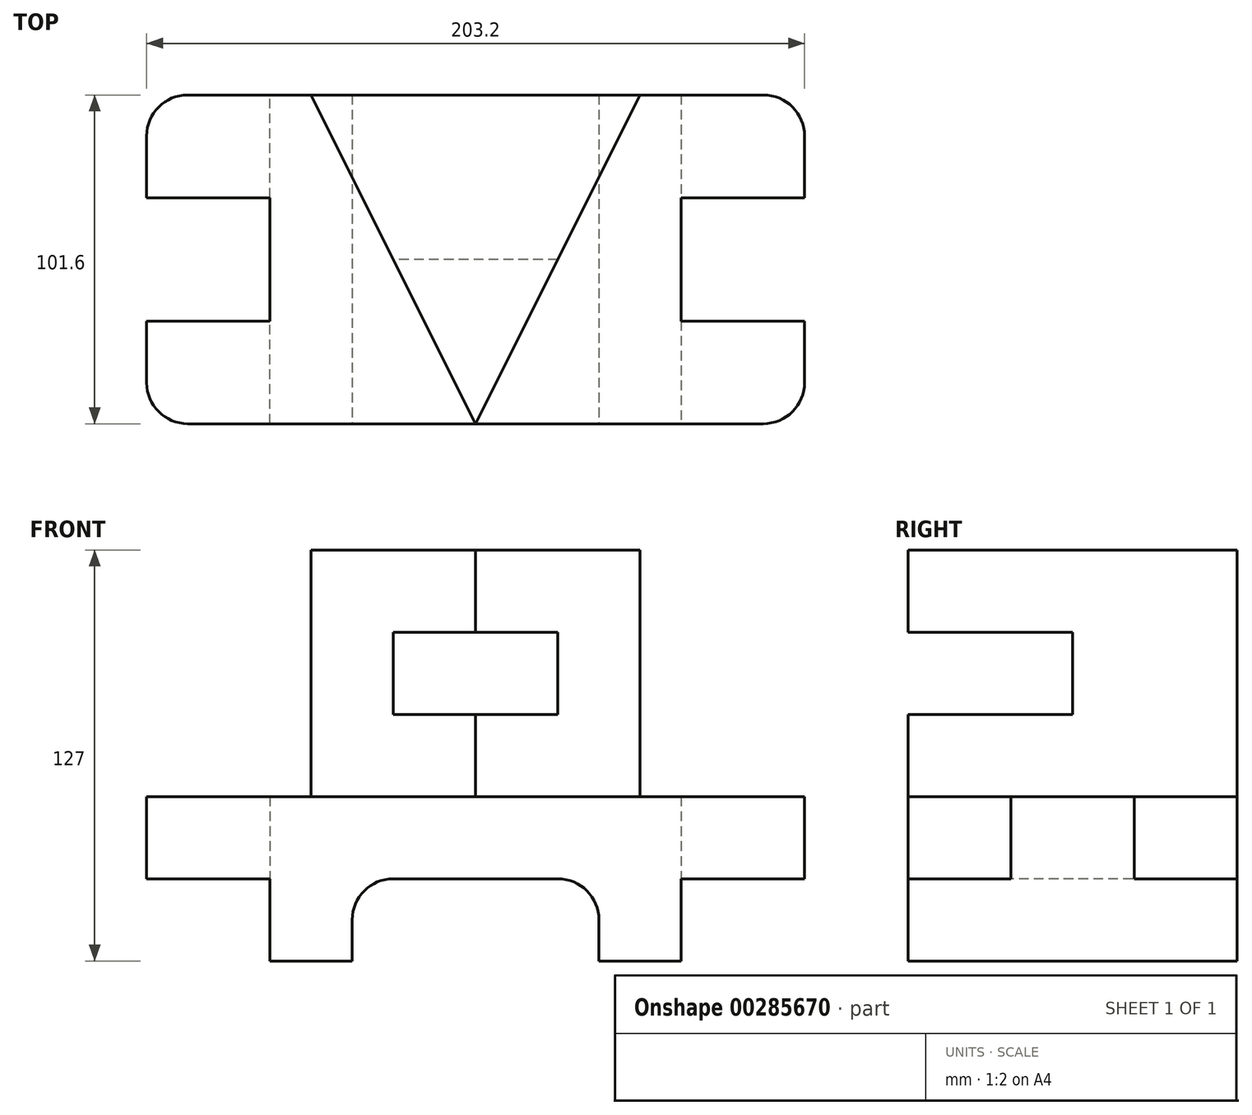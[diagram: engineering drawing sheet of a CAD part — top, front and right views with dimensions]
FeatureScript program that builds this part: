
annotation { "Feature Type Name" : "Feature", "Feature Type Description" : "" }
export const myFeature = defineFeature(function(context is Context, id is Id, definition is map)
    precondition{}
    {
        {
            var Q0;
            Q0=qCreatedBy(makeId("Top.planeOp"),FACE);
            var sketch = newSketch(context, id + "F0", { "sketchPlane" : qUnion([Q0])});
            skLineSegment(sketch, "E0", {"start": v(0, 0) * mm, "end": v(177.8, 0) * mm});
            skLineSegment(sketch, "E1", {"start": v(0, 0) * mm, "end": v(0, 31.75) * mm});
            skLineSegment(sketch, "E2", {"start": v(0, 31.75) * mm, "end": v(25.4, 31.75) * mm});
            skLineSegment(sketch, "E3", {"start": v(25.4, 31.75) * mm, "end": v(25.4, 69.85) * mm});
            skLineSegment(sketch, "E4", {"start": v(25.4, 69.85) * mm, "end": v(0, 69.85) * mm});
            skLineSegment(sketch, "E5", {"start": v(0, 69.85) * mm, "end": v(0, 101.6) * mm});
            skLineSegment(sketch, "E6", {"start": v(0, 101.6) * mm, "end": v(177.8, 101.6) * mm});
            skLineSegment(sketch, "E7", {"start": v(177.8, 101.6) * mm, "end": v(177.8, 69.85) * mm});
            skLineSegment(sketch, "E8", {"start": v(177.8, 69.85) * mm, "end": v(152.4, 69.85) * mm});
            skLineSegment(sketch, "E9", {"start": v(152.4, 69.85) * mm, "end": v(152.4, 31.75) * mm});
            skLineSegment(sketch, "E10", {"start": v(152.4, 31.75) * mm, "end": v(177.8, 31.75) * mm});
            skLineSegment(sketch, "E11", {"start": v(177.8, 31.75) * mm, "end": v(177.8, 0) * mm});
            skLineSegment(sketch, "E12", {"start": v(0, 31.75) * mm, "end": v(-12.7, 31.75) * mm});
            skLineSegment(sketch, "E13", {"start": v(-12.7, 31.75) * mm, "end": v(-12.7, 12.7) * mm});
            skLineSegment(sketch, "E14", {"start": v(177.8, 31.75) * mm, "end": v(190.5, 31.75) * mm});
            skPoint(sketch, "E14.endSnap0", {"position": v(165.1, 31.75) * mm});
            skLineSegment(sketch, "E15", {"start": v(190.5, 31.75) * mm, "end": v(190.5, 12.7) * mm});
            skLineSegment(sketch, "E16", {"start": v(177.8, 69.85) * mm, "end": v(190.5, 69.85) * mm});
            skLineSegment(sketch, "E17", {"start": v(0, 69.85) * mm, "end": v(-12.7, 69.85) * mm});
            skLineSegment(sketch, "E18", {"start": v(-12.7, 69.85) * mm, "end": v(-12.7, 88.9) * mm});
            skLineSegment(sketch, "E19", {"start": v(190.5, 69.85) * mm, "end": v(190.5, 88.9) * mm});
            skArc(sketch, "E20", {"start": v(0, 101.6) * mm, "mid": v(-8.98, 97.88) * mm, "end": v(-12.7, 88.9) * mm});
            skArc(sketch, "E21", {"start": v(-12.7, 12.7) * mm, "mid": v(-8.98, 3.72) * mm, "end": v(0, 0) * mm});
            skArc(sketch, "E22", {"start": v(177.8, 0) * mm, "mid": v(186.78, 3.72) * mm, "end": v(190.5, 12.7) * mm});
            skArc(sketch, "E23", {"start": v(190.5, 88.9) * mm, "mid": v(186.78, 97.88) * mm, "end": v(177.8, 101.6) * mm});
            skSolve(sketch);
        }
        {
            var Q0;
            Q0 = qSketchRegion(id + "F0", true);
            extrude(context, id + "F1", {"entities" : qUnion([Q0]), "depth" : 25.4 * mm});
        }
        {
            var Q0;
            Q0=makeQuery(id+"F1.opExtrude","CAP_FACE",FACE,{"disambiguationData":[OSD([sQuery(id+"F0.wireOp",EDGE,"E0"),sQuery(id+"F0.wireOp",EDGE,"E2"),sQuery(id+"F0.wireOp",EDGE,"E3"),sQuery(id+"F0.wireOp",EDGE,"E4"),sQuery(id+"F0.wireOp",EDGE,"E6"),sQuery(id+"F0.wireOp",EDGE,"E8"),sQuery(id+"F0.wireOp",EDGE,"E9"),sQuery(id+"F0.wireOp",EDGE,"E10"),sQuery(id+"F0.wireOp",EDGE,"E12"),sQuery(id+"F0.wireOp",EDGE,"E13"),sQuery(id+"F0.wireOp",EDGE,"E14"),sQuery(id+"F0.wireOp",EDGE,"E15"),sQuery(id+"F0.wireOp",EDGE,"E16"),sQuery(id+"F0.wireOp",EDGE,"E17"),sQuery(id+"F0.wireOp",EDGE,"E18"),sQuery(id+"F0.wireOp",EDGE,"E19"),sQuery(id+"F0.wireOp",EDGE,"E20"),sQuery(id+"F0.wireOp",EDGE,"E21"),sQuery(id+"F0.wireOp",EDGE,"E22"),sQuery(id+"F0.wireOp",EDGE,"E23")])],"isStart":false});
            var sketch = newSketch(context, id + "F2", { "sketchPlane" : qUnion([Q0])});
            skLineSegment(sketch, "E24", {"start": v(88.9, 0) * mm, "end": v(139.7, 101.6) * mm});
            skLineSegment(sketch, "E25", {"start": v(88.9, 0) * mm, "end": v(38.1, 101.6) * mm});
            skLineSegment(sketch, "E26", {"start": v(38.1, 101.6) * mm, "end": v(139.7, 101.6) * mm});
            skSolve(sketch);
        }
        {
            var Q0;
            Q0 = qSketchRegion(id + "F2", true);
            extrude(context, id + "F3", {"entities" : qUnion([Q0]), "operationType" : NewBodyOperationType.ADD, "depth" : 25.4 * mm});
        }
        {
            var Q0;
            Q0=makeQuery(id+"F3.opExtrude","CAP_FACE",FACE,{"disambiguationData":[OSD([sQuery(id+"F2.wireOp",EDGE,"E24"),sQuery(id+"F2.wireOp",EDGE,"E25"),sQuery(id+"F2.wireOp",EDGE,"E26")])],"isStart":false});
            var sketch = newSketch(context, id + "F4", { "sketchPlane" : qUnion([Q0])});
            skLineSegment(sketch, "E27", {"start": v(38.1, 101.6) * mm, "end": v(139.7, 101.6) * mm});
            skLineSegment(sketch, "E28", {"start": v(139.7, 101.6) * mm, "end": v(114.3, 50.8) * mm});
            skLineSegment(sketch, "E29", {"start": v(114.3, 50.8) * mm, "end": v(63.5, 50.8) * mm});
            skLineSegment(sketch, "E30", {"start": v(63.5, 50.8) * mm, "end": v(38.1, 101.6) * mm});
            skSolve(sketch);
        }
        {
            var Q0;
            Q0 = qSketchRegion(id + "F4", true);
            extrude(context, id + "F5", {"entities" : qUnion([Q0]), "operationType" : NewBodyOperationType.ADD, "depth" : 25.4 * mm});
        }
        {
            var Q0;
            Q0=makeQuery(id+"F5.opExtrude","CAP_FACE",FACE,{"disambiguationData":[OSD([sQuery(id+"F4.wireOp",EDGE,"E27"),sQuery(id+"F4.wireOp",EDGE,"E28"),sQuery(id+"F4.wireOp",EDGE,"E29"),sQuery(id+"F4.wireOp",EDGE,"E30")])],"isStart":false});
            var sketch = newSketch(context, id + "F6", { "sketchPlane" : qUnion([Q0])});
            skLineSegment(sketch, "E31", {"start": v(38.1, 101.6) * mm, "end": v(139.7, 101.6) * mm});
            skLineSegment(sketch, "E32", {"start": v(139.7, 101.6) * mm, "end": v(88.9, 0) * mm});
            skLineSegment(sketch, "E33", {"start": v(88.9, 0) * mm, "end": v(38.1, 101.6) * mm});
            skSolve(sketch);
        }
        {
            var Q0;
            Q0 = qSketchRegion(id + "F6", true);
            extrude(context, id + "F7", {"entities" : qUnion([Q0]), "operationType" : NewBodyOperationType.ADD, "depth" : 25.4 * mm});
        }
        {
            var Q0;
            Q0=makeQuery(id+"F1.opExtrude","CAP_FACE",FACE,{"disambiguationData":[OSD([sQuery(id+"F0.wireOp",EDGE,"E0"),sQuery(id+"F0.wireOp",EDGE,"E2"),sQuery(id+"F0.wireOp",EDGE,"E3"),sQuery(id+"F0.wireOp",EDGE,"E4"),sQuery(id+"F0.wireOp",EDGE,"E6"),sQuery(id+"F0.wireOp",EDGE,"E8"),sQuery(id+"F0.wireOp",EDGE,"E9"),sQuery(id+"F0.wireOp",EDGE,"E10"),sQuery(id+"F0.wireOp",EDGE,"E12"),sQuery(id+"F0.wireOp",EDGE,"E13"),sQuery(id+"F0.wireOp",EDGE,"E14"),sQuery(id+"F0.wireOp",EDGE,"E15"),sQuery(id+"F0.wireOp",EDGE,"E16"),sQuery(id+"F0.wireOp",EDGE,"E17"),sQuery(id+"F0.wireOp",EDGE,"E18"),sQuery(id+"F0.wireOp",EDGE,"E19"),sQuery(id+"F0.wireOp",EDGE,"E20"),sQuery(id+"F0.wireOp",EDGE,"E21"),sQuery(id+"F0.wireOp",EDGE,"E22"),sQuery(id+"F0.wireOp",EDGE,"E23")])],"isStart":true});
            var sketch = newSketch(context, id + "F8", { "sketchPlane" : qUnion([Q0])});
            skLineSegment(sketch, "E34", {"start": v(25.4, 0) * mm, "end": v(25.4, -101.6) * mm});
            skLineSegment(sketch, "E35", {"start": v(25.4, 0) * mm, "end": v(50.8, 0) * mm});
            skLineSegment(sketch, "E36", {"start": v(50.8, 0) * mm, "end": v(50.8, -101.6) * mm});
            skLineSegment(sketch, "E37", {"start": v(50.8, -101.6) * mm, "end": v(25.4, -101.6) * mm});
            skLineSegment(sketch, "E38", {"start": v(152.4, -101.6) * mm, "end": v(152.4, 0) * mm});
            skLineSegment(sketch, "E39", {"start": v(152.4, 0) * mm, "end": v(127, 0) * mm});
            skLineSegment(sketch, "E40", {"start": v(127, 0) * mm, "end": v(127, -101.6) * mm});
            skLineSegment(sketch, "E41", {"start": v(127, -101.6) * mm, "end": v(152.4, -101.6) * mm});
            skSolve(sketch);
        }
        {
            var Q0;
            Q0 = qSketchRegion(id + "F8", true);
            extrude(context, id + "F9", {"entities" : qUnion([Q0]), "operationType" : NewBodyOperationType.ADD, "depth" : 25.4 * mm});
        }
        {
            var Q0;
            Q0=makeQuery(id+"F9.boolean.opBoolean","MERGE",FACE,{"derivedFrom":[makeQuery(id+"F1.opExtrude","SWEPT_FACE",FACE,{"disambiguationData":[OSD([sQuery(id+"F0.wireOp",EDGE,"E0")])]}),makeQuery(id+"F9.opExtrude","SWEPT_FACE",FACE,{"disambiguationData":[OSD([sQuery(id+"F8.wireOp",EDGE,"E35")])]}),makeQuery(id+"F9.opExtrude","SWEPT_FACE",FACE,{"disambiguationData":[OSD([sQuery(id+"F8.wireOp",EDGE,"E39")])]})]});
            var sketch = newSketch(context, id + "F10", { "sketchPlane" : qUnion([Q0])});
            skLineSegment(sketch, "E42", {"start": v(50.8, 0) * mm, "end": v(63.5, 0) * mm});
            skLineSegment(sketch, "E43", {"start": v(50.8, 0) * mm, "end": v(50.8, -12.7) * mm});
            skLineSegment(sketch, "E44", {"start": v(127, 0) * mm, "end": v(127, -12.7) * mm});
            skLineSegment(sketch, "E45", {"start": v(127, 0) * mm, "end": v(114.3, 0) * mm});
            skArc(sketch, "E46", {"start": v(63.5, 0) * mm, "mid": v(54.52, -3.72) * mm, "end": v(50.8, -12.7) * mm});
            skArc(sketch, "E47", {"start": v(127, -12.7) * mm, "mid": v(123.28, -3.72) * mm, "end": v(114.3, 0) * mm});
            skSolve(sketch);
        }
        {
            var Q0;
            Q0=makeQuery(id+"F10.imprint","IMPRINT",FACE,{"disambiguationData":[TD([[makeQuery(id+"F10.imprint","IMPRINT",EDGE,{"derivedFrom":sQuery(id+"F10.wireOp",EDGE,"E42")}),-1.0]])]});
            var Q1;
            Q1=makeQuery(id+"F10.imprint","IMPRINT",FACE,{"disambiguationData":[TD([[makeQuery(id+"F10.imprint","IMPRINT",EDGE,{"derivedFrom":sQuery(id+"F10.wireOp",EDGE,"E44")}),1.0]])]});
            extrude(context, id + "F11", {"entities" : qUnion([Q0, Q1]), "operationType" : NewBodyOperationType.ADD, "oppositeDirection" : true, "depth" : 101.6 * mm});
        }
    });
